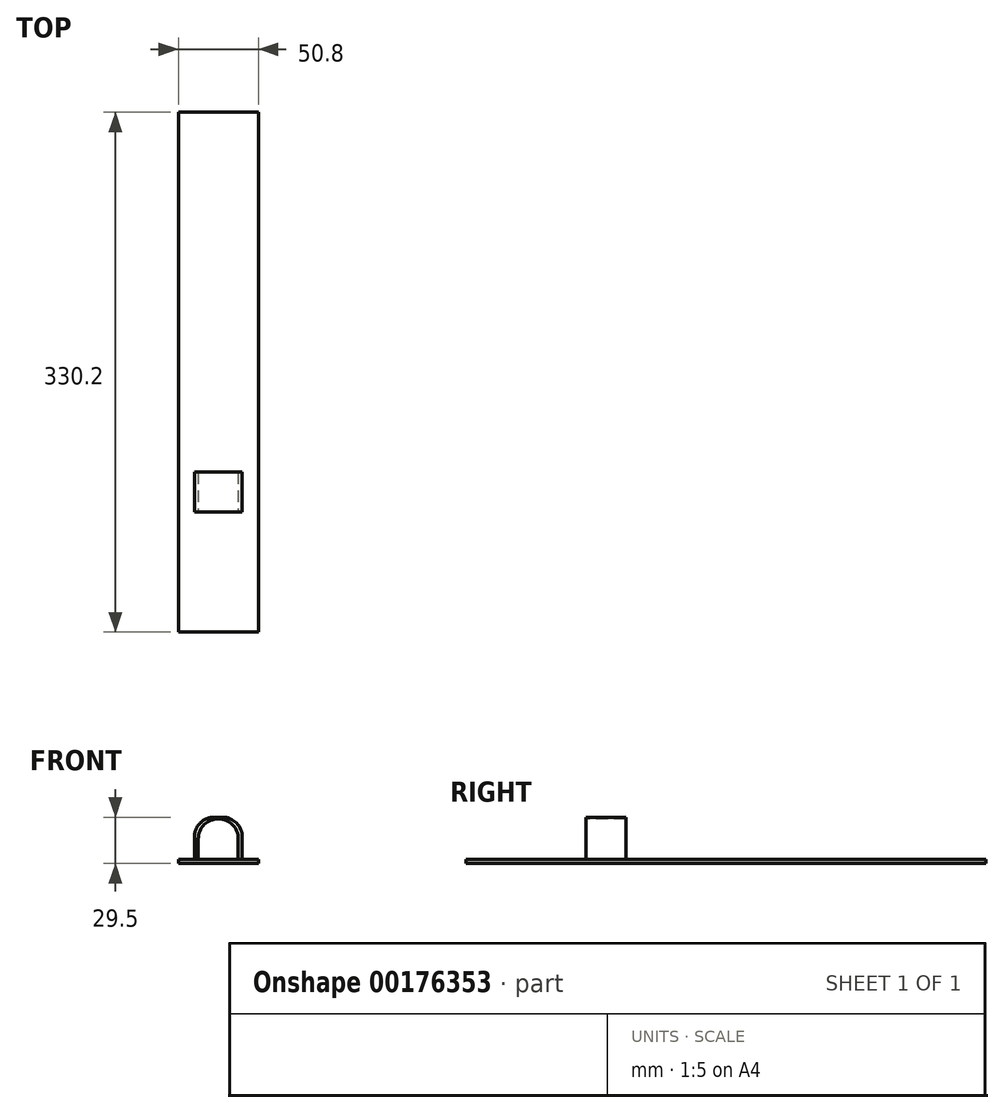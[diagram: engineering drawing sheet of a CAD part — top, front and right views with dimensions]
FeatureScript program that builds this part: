
annotation { "Feature Type Name" : "Feature", "Feature Type Description" : "" }
export const myFeature = defineFeature(function(context is Context, id is Id, definition is map)
    precondition{}
    {
        {
            var Q0;
            Q0=qCreatedBy(makeId("Front.planeOp"),FACE);
            var sketch = newSketch(context, id + "F0", { "sketchPlane" : qUnion([Q0])});
            skCircle(sketch, "E0", {"center": v(0, 0) * mm, "radius": 12.7 * mm, "construction": true});
            skLineSegment(sketch, "E1", {"start": v(-25.35, -13.14) * mm, "end": v(25.45, -13.14) * mm});
            skLineSegment(sketch, "E2", {"start": v(25.45, -13.14) * mm, "end": v(25.45, -15.7) * mm});
            skLineSegment(sketch, "E3", {"start": v(25.45, -15.7) * mm, "end": v(-25.35, -15.7) * mm});
            skLineSegment(sketch, "E4", {"start": v(-25.35, -15.7) * mm, "end": v(-25.35, -13.14) * mm});
            skLineSegment(sketch, "E5", {"start": v(-12.76, -13.14) * mm, "end": v(-12.7, 0.13) * mm});
            skLineSegment(sketch, "E6", {"start": v(0.05, 12.78) * mm, "end": v(0.1, 12.78) * mm});
            skLineSegment(sketch, "E7", {"start": v(12.75, 0.08) * mm, "end": v(12.75, -13.14) * mm});
            skPoint(sketch, "E8.visualSharp", {"position": v(-12.64, 12.83) * mm});
            skArc(sketch, "E8.filletArc", {"start": v(0.05, 12.78) * mm, "mid": v(-8.94, 9.1) * mm, "end": v(-12.7, 0.13) * mm});
            skPoint(sketch, "E9.visualSharp", {"position": v(12.75, 12.72) * mm});
            skArc(sketch, "E9.filletArc", {"start": v(12.75, 0.08) * mm, "mid": v(9.05, 9.04) * mm, "end": v(0.1, 12.78) * mm});
            skLineSegment(sketch, "E10", {"start": v(-15.18, -13.14) * mm, "end": v(-15.18, 1.1) * mm});
            skLineSegment(sketch, "E11", {"start": v(-2.43, 13.8) * mm, "end": v(2.65, 13.78) * mm});
            skLineSegment(sketch, "E12", {"start": v(15.3, 1.08) * mm, "end": v(15.3, -13.14) * mm});
            skPoint(sketch, "E13.visualSharp", {"position": v(15.3, 13.73) * mm});
            skArc(sketch, "E13.filletArc", {"start": v(15.3, 1.08) * mm, "mid": v(11.6, 10.05) * mm, "end": v(2.65, 13.78) * mm});
            skPoint(sketch, "E14.visualSharp", {"position": v(-15.18, 13.86) * mm});
            skArc(sketch, "E14.filletArc", {"start": v(-2.43, 13.8) * mm, "mid": v(-11.45, 10.1) * mm, "end": v(-15.18, 1.1) * mm});
            skSolve(sketch);
        }
        {
            var Q0;
            {var subQ6=sQuery(id+"F0.wireOp",EDGE,"E2");Q0=makeQuery(id+"F0.imprint","IMPRINT",FACE,{"disambiguationData":[TD([[makeQuery(id+"F0.imprint","IMPRINT",EDGE,{"derivedFrom":subQ6}),-1.0]])]});}
            extrude(context, id + "F1", {"entities" : qUnion([Q0]), "depth" : 76.2 * mm});
        }
        {
            var Q0;
            {var subQ6=sQuery(id+"F0.wireOp",EDGE,"E2");Q0=makeQuery(id+"F0.imprint","IMPRINT",FACE,{"disambiguationData":[TD([[makeQuery(id+"F0.imprint","IMPRINT",EDGE,{"derivedFrom":subQ6}),-1.0]])]});}
            extrude(context, id + "F2", {"entities" : qUnion([Q0]), "operationType" : NewBodyOperationType.ADD, "oppositeDirection" : true, "depth" : 254 * mm});
        }
        {
            var Q0;
            {var subQ1=sQuery(id+"F0.wireOp",EDGE,"E5");Q0=makeQuery(id+"F0.imprint","IMPRINT",FACE,{"disambiguationData":[TD([[makeQuery(id+"F0.imprint","IMPRINT",EDGE,{"derivedFrom":subQ1}),1.0]])]});}
            extrude(context, id + "F3", {"entities" : qUnion([Q0]), "operationType" : NewBodyOperationType.ADD, "oppositeDirection" : true, "depth" : 25.4 * mm});
        }
    });
